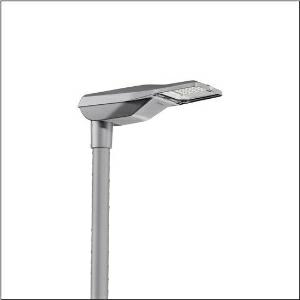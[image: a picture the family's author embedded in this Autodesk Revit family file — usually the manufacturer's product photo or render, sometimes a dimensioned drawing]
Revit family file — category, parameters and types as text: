
# Revit family: streetlight_sl_21_iq_micro___st1_0a_5xe1d31g08db_9cf9
name_source: partatom
category: Lighting Fixtures
units: mm (PartAtom-declared; Revit-internal decimal feet)

## family parameters
Cut with Voids When Loaded = No
Host = Face
Light Source = No
Part Type = Normal
Room Calculation Point = No
Round Connector Dimension = Use Diameter
Shared = No

## types (1)
- --- (1 x LED, 4810 lm, 36.4 W, 3000K)
    Apparent Load = 36 VA
    CIE Flux Codes = 37 72 97 100 100
    Color Rendering = 70
    Color Temperature = 3000K
    Default Elevation = 1800 mm
    Description = Streetlight SL 21 iQ micro, mast luminaire, primary light control with lens, of PMMA, primary optical cover: cover, of toughened safety glass, transparent, light distribution: ST1.0a, light emission: direct distribution, primary light characteristic: asymmetric, installation type: post-top, side-entry, LED, High Power LED, rated luminous flux: 4.810lm, luminous efficacy: 132lm/W, light colour: 730, colour temperature: 3000K, control gear: iQ Street-Remote, control: Street-Remote, Auto-Match, Temp-Guard, Lumen-Switch, Night-Set, Smart-Wire, Light-Fading, Desk-Remote (wireless, voltage-free reading and setting of iQ features in the workshop via application-optimized NFC function/RFID function), optimised constant luminous flux control (CLO 2.0), pre-setting: linear dimming characteristic, mains connection: 220..240V, AC, 50/60Hz, start of lifetime: 36W, end of service life: 38W, reduction: 16W, luminaire housing, of diecast aluminium, powder-coated, SITECO metallic grey (DB 702S), corrosivity category C5 high according to DIN EN ISO 12944, please order mast flange separately, inclination adjustable: 0°, 5°, 10°, 15°, sealing non-destructively replaceable, multi-level sealing system, length: 528mm, width: 235mm, height: 110mm, mast flange for spigot size: 42mm (side-entry): 5XC10008XM4, 60/48mm (side-entry/post-top): 5XC10108XM2, 76/60mm (side-entry/post-top): 5XC10108XM1, protection rating (complete): IP66, insulation class (complete): insulation class II (safety insulation), certification: CE, ENEC, ENEC+, VDE, impact resistance: IK10, permissible operating ambient temperature for outdoor applications: -40..+50°C, standard-compliant lighting for roads and squares, packaging unit: 1 piece

Light Distribution: ST1.0a
    Height = 110 mm
    Lamp = 1 x LED
    Lamp Light Flux = 4810 lm
    Lamp Power = 36.4 W
    Lamp count = 1
    Length = 528 mm
    Luminous efficacy = 132 lm/W
    Manufacturer = Siteco
    ModVariant = No
    Model = 5XE1D31G08DB
    Number of Poles = 1
    OnlyDefault = Yes
    Power Factor = 1
    Product Name = Streetlight SL 21 iQ micro | ST1.0a
    Product group = mast luminaire | pylon top
    ProductGroupID = 6100
    Protection Class = Protection class II
    Protection Degree = IP 66
    RLX_Detail_Level = 1
    RLX_Emergency_Light_Flux = 0 lm
    RLX_Emergency_Type = 0
    RLX_Emergency_Type_DB = No
    RlxData = <blob elided: 99393 chars, md5=eb69b04d>
    Socket = socket
    Standby Power = 0 W
    System Light Flux = 4810 lm
    System Power = 36 W
    Type Comments = factory setting: luminous flux: 100 % | dim-lin: 254 | 715 mA
    Type Image = l_1006881.jpg
    URL = http://relux.com
    VarID = @adj_155479
    Voltage = 0 V
    Weight = 0.00 kg
    Width = 235 mm

## geometry (parser evidence)
native form markers: Blend x4, Sweep x13
no freeform markers — native parametric forms only
